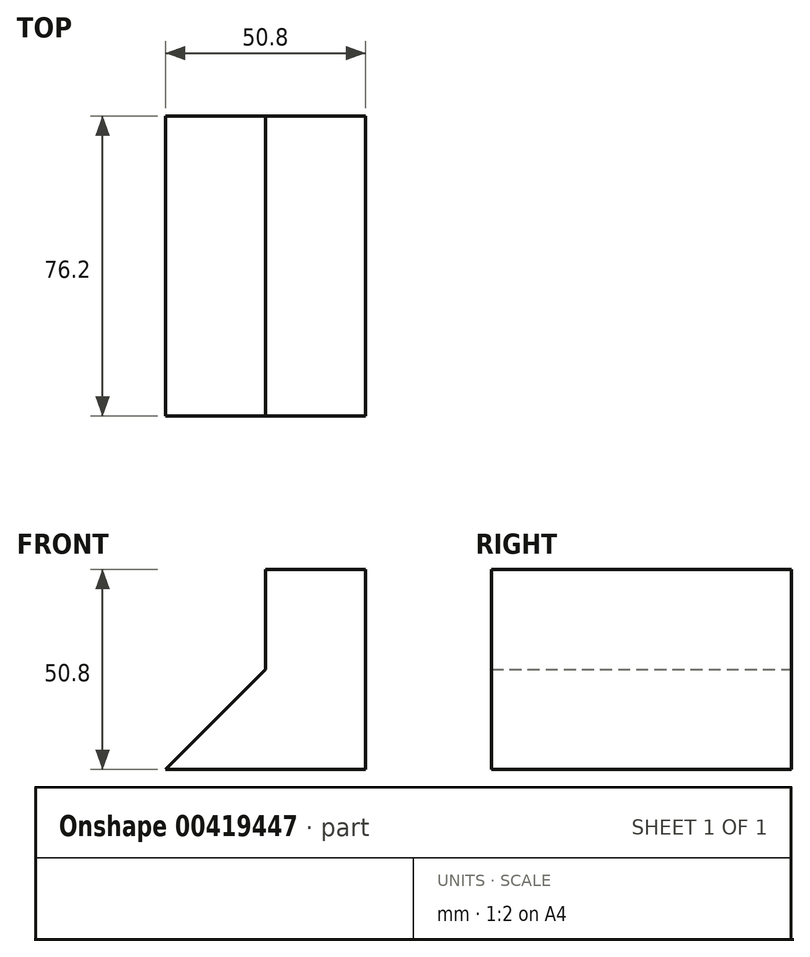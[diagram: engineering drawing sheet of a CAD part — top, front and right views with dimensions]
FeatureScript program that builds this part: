
annotation { "Feature Type Name" : "Feature", "Feature Type Description" : "" }
export const myFeature = defineFeature(function(context is Context, id is Id, definition is map)
    precondition{}
    {
        {
            var Q0;
            Q0=qCreatedBy(makeId("Front.planeOp"),FACE);
            var sketch = newSketch(context, id + "F0", { "sketchPlane" : qUnion([Q0])});
            skLineSegment(sketch, "E0", {"start": v(18.14, 17.82) * mm, "end": v(18.14, -32.98) * mm});
            skLineSegment(sketch, "E1", {"start": v(18.14, -32.98) * mm, "end": v(-32.66, -32.98) * mm});
            skLineSegment(sketch, "E2", {"start": v(18.14, 17.82) * mm, "end": v(-7.26, 17.82) * mm});
            skLineSegment(sketch, "E3", {"start": v(-7.26, 17.82) * mm, "end": v(-7.26, -7.58) * mm});
            skLineSegment(sketch, "E4", {"start": v(-7.26, -7.58) * mm, "end": v(-32.66, -32.98) * mm});
            skSolve(sketch);
        }
        {
            var Q0;
            Q0=makeQuery(id+"F0.imprint","IMPRINT",FACE,{"disambiguationData":[TD([[makeQuery(id+"F0.imprint","IMPRINT",EDGE,{"derivedFrom":sQuery(id+"F0.wireOp",EDGE,"E0")}),-1.0]])]});
            extrude(context, id + "F1", {"entities" : qUnion([Q0]), "depth" : 76.2 * mm});
        }
    });
